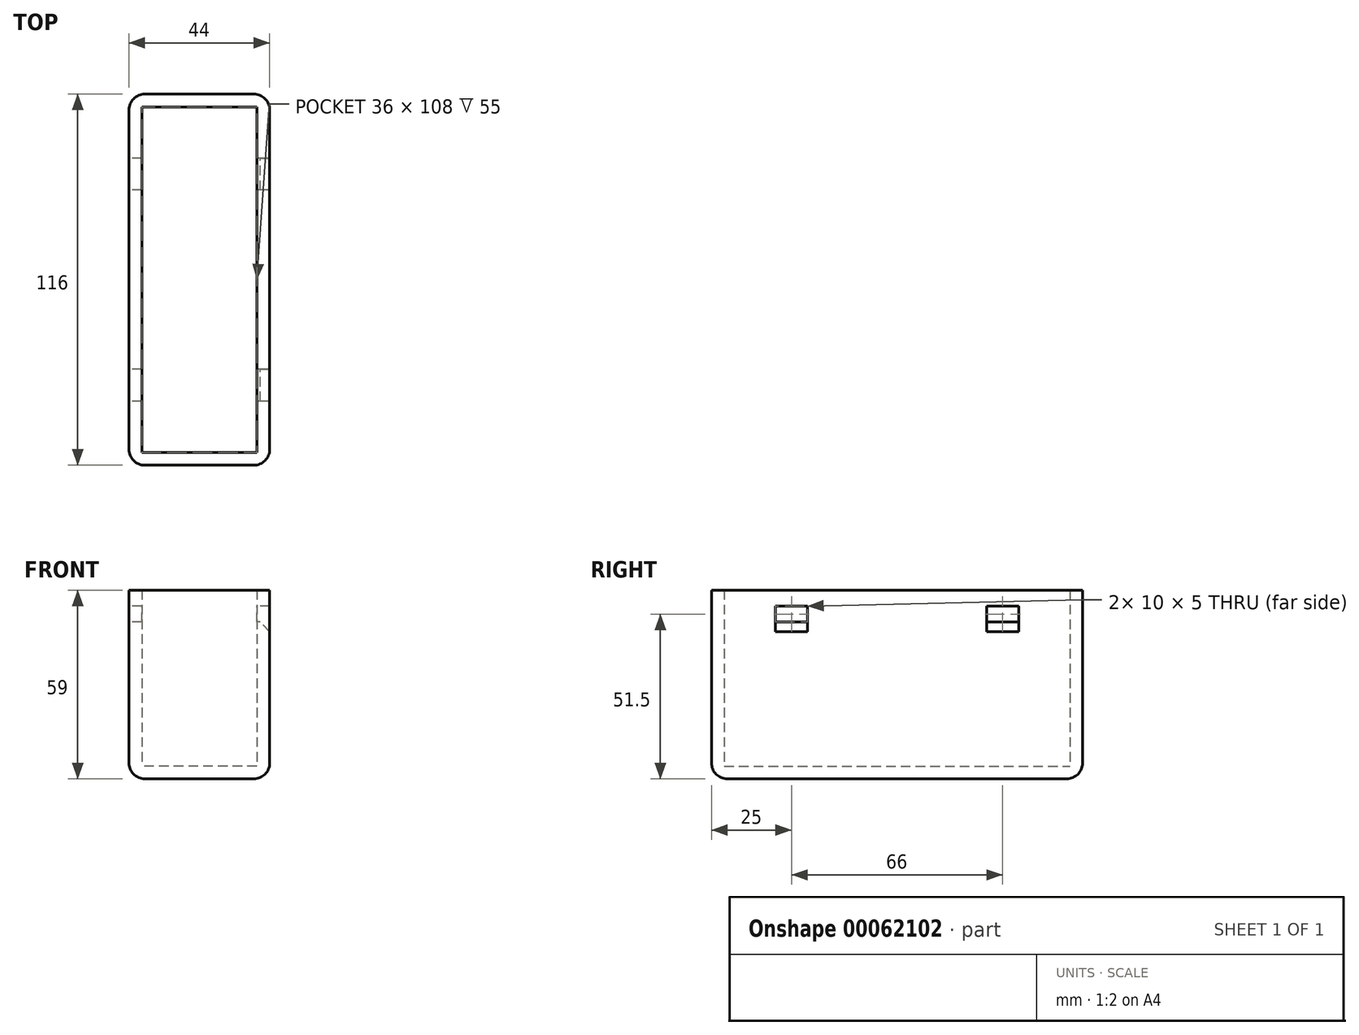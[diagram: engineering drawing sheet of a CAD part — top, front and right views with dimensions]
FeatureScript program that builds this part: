
annotation { "Feature Type Name" : "Feature", "Feature Type Description" : "" }
export const myFeature = defineFeature(function(context is Context, id is Id, definition is map)
    precondition{}
    {
        {
            var Q0;
            Q0=qCreatedBy(makeId("Top.planeOp"),FACE);
            var sketch = newSketch(context, id + "F0", { "sketchPlane" : qUnion([Q0])});
            skLineSegment(sketch, "E0.rect.bottom", {"start": v(18, -54) * mm, "end": v(-18, -54) * mm});
            skLineSegment(sketch, "E0.rect.top", {"start": v(18, 54) * mm, "end": v(-18, 54) * mm});
            skLineSegment(sketch, "E0.rect.left", {"start": v(18, -54) * mm, "end": v(18, 54) * mm});
            skLineSegment(sketch, "E0.rect.right", {"start": v(-18, -54) * mm, "end": v(-18, 54) * mm});
            skPoint(sketch, "E0.rect.middle", {"position": v(0, 0) * mm});
            skSolve(sketch);
        }
        {
            var Q0;
            Q0=makeQuery(id+"F0.imprint","IMPRINT",FACE,{"disambiguationData":[TD([[makeQuery(id+"F0.imprint","IMPRINT",EDGE,{"derivedFrom":sQuery(id+"F0.wireOp",EDGE,"E0.rect.bottom")}),-1.0]])]});
            extrude(context, id + "F1", {"entities" : qUnion([Q0]), "depth" : 55 * mm});
        }
        {
            var Q0;
            Q0=makeQuery(id+"F1.opExtrude","CAP_FACE",FACE,{"disambiguationData":[OSD([sQuery(id+"F0.wireOp",EDGE,"E0.rect.bottom"),sQuery(id+"F0.wireOp",EDGE,"E0.rect.top"),sQuery(id+"F0.wireOp",EDGE,"E0.rect.left"),sQuery(id+"F0.wireOp",EDGE,"E0.rect.right")])],"isStart":false});
            shell(context, id + "F2", {"entities" : qUnion([Q0]), "thickness" : 4 * mm, "oppositeDirection" : true});
        }
        {
            var Q0;
            Q0=makeQuery(id+"F1.opExtrude","SWEPT_EDGE",EDGE,{"disambiguationData":[OSD([sQuery(id+"F0.wireOp",EDGE,"E0.rect.bottom"),sQuery(id+"F0.wireOp",EDGE,"E0.rect.right")])]});
            var Q1;
            Q1=makeQuery(id+"F1.opExtrude","SWEPT_EDGE",EDGE,{"disambiguationData":[OSD([sQuery(id+"F0.wireOp",EDGE,"E0.rect.bottom"),sQuery(id+"F0.wireOp",EDGE,"E0.rect.left")])]});
            var Q2;
            Q2=makeQuery(id+"F1.opExtrude","SWEPT_EDGE",EDGE,{"disambiguationData":[OSD([sQuery(id+"F0.wireOp",EDGE,"E0.rect.top"),sQuery(id+"F0.wireOp",EDGE,"E0.rect.right")])]});
            var Q3;
            Q3=makeQuery(id+"F1.opExtrude","SWEPT_EDGE",EDGE,{"disambiguationData":[OSD([sQuery(id+"F0.wireOp",EDGE,"E0.rect.top"),sQuery(id+"F0.wireOp",EDGE,"E0.rect.left")])]});
            var Q4;
            Q4=makeQuery(id+"F1.opExtrude","CAP_FACE",FACE,{"disambiguationData":[OSD([sQuery(id+"F0.wireOp",EDGE,"E0.rect.bottom"),sQuery(id+"F0.wireOp",EDGE,"E0.rect.top"),sQuery(id+"F0.wireOp",EDGE,"E0.rect.left"),sQuery(id+"F0.wireOp",EDGE,"E0.rect.right")])],"isStart":true});
            fillet(context, id + "F3", {"entities" : qUnion([Q0, Q1, Q2, Q3, Q4]), "radius" : 5 * mm, "tangentPropagation" : true, "allowEdgeOverflow" : false});
        }
        {
            var Q0;
            Q0=makeQuery(id+"F1.opExtrude","SWEPT_FACE",FACE,{"disambiguationData":[OSD([sQuery(id+"F0.wireOp",EDGE,"E0.rect.right")])]});
            var sketch = newSketch(context, id + "F4", { "sketchPlane" : qUnion([Q0])});
            skLineSegment(sketch, "E1.rect.bottom", {"start": v(-28, 45) * mm, "end": v(-38, 45) * mm});
            skLineSegment(sketch, "E1.rect.top", {"start": v(-28, 50) * mm, "end": v(-38, 50) * mm});
            skLineSegment(sketch, "E1.rect.left", {"start": v(-28, 45) * mm, "end": v(-28, 50) * mm});
            skLineSegment(sketch, "E1.rect.right", {"start": v(-38, 45) * mm, "end": v(-38, 50) * mm});
            skPoint(sketch, "E1.rect.middle", {"position": v(-33, 47.5) * mm});
            skLineSegment(sketch, "E2.rect.bottom", {"start": v(38, 45) * mm, "end": v(28, 45) * mm});
            skLineSegment(sketch, "E2.rect.top", {"start": v(38, 50) * mm, "end": v(28, 50) * mm});
            skLineSegment(sketch, "E2.rect.left", {"start": v(38, 45) * mm, "end": v(38, 50) * mm});
            skLineSegment(sketch, "E2.rect.right", {"start": v(28, 45) * mm, "end": v(28, 50) * mm});
            skPoint(sketch, "E2.rect.middle", {"position": v(33, 47.5) * mm});
            skSolve(sketch);
        }
        {
            var Q0;
            Q0=makeQuery(id+"F4.imprint","IMPRINT",FACE,{"disambiguationData":[TD([[makeQuery(id+"F4.imprint","IMPRINT",EDGE,{"derivedFrom":sQuery(id+"F4.wireOp",EDGE,"E1.rect.bottom")}),-1.0]])]});
            var Q1;
            Q1=makeQuery(id+"F4.imprint","IMPRINT",FACE,{"disambiguationData":[TD([[makeQuery(id+"F4.imprint","IMPRINT",EDGE,{"derivedFrom":sQuery(id+"F4.wireOp",EDGE,"E2.rect.bottom")}),-1.0]])]});
            extrude(context, id + "F5", {"entities" : qUnion([Q0, Q1]), "operationType" : NewBodyOperationType.REMOVE, "endBound" : BoundingType.THROUGH_ALL, "oppositeDirection" : true, "depth" : 25 * mm});
        }
        {
            var Q0;
            Q0=makeQuery(id+"F5.boolean.opBoolean","COPY",EDGE,{"derivedFrom":makeQuery(id+"F5.opExtrude","CAP_EDGE",EDGE,{"disambiguationData":[OSD([sQuery(id+"F4.wireOp",EDGE,"E1.rect.bottom")])],"isStart":true})});
            var Q1;
            Q1=makeQuery(id+"F5.boolean.opBoolean","COPY",EDGE,{"derivedFrom":makeQuery(id+"F5.opExtrude","CAP_EDGE",EDGE,{"disambiguationData":[OSD([sQuery(id+"F4.wireOp",EDGE,"E2.rect.bottom")])],"isStart":true})});
            var Q2;
            Q2=makeQuery(id+"F5.boolean.opBoolean","INTERSECT",EDGE,{"derivedFrom":[makeQuery(id+"F1.opExtrude","SWEPT_FACE",FACE,{"disambiguationData":[OSD([sQuery(id+"F0.wireOp",EDGE,"E0.rect.left")])]}),makeQuery(id+"F5.opExtrude","SWEPT_FACE",FACE,{"disambiguationData":[OSD([sQuery(id+"F4.wireOp",EDGE,"E2.rect.bottom")])]})]});
            var Q3;
            Q3=makeQuery(id+"F5.boolean.opBoolean","INTERSECT",EDGE,{"derivedFrom":[makeQuery(id+"F1.opExtrude","SWEPT_FACE",FACE,{"disambiguationData":[OSD([sQuery(id+"F0.wireOp",EDGE,"E0.rect.left")])]}),makeQuery(id+"F5.opExtrude","SWEPT_FACE",FACE,{"disambiguationData":[OSD([sQuery(id+"F4.wireOp",EDGE,"E1.rect.bottom")])]})]});
            chamfer(context, id + "F6", {"entities" : qUnion([Q0, Q1, Q2, Q3]), "width" : 3 * mm, "tangentPropagation" : true});
        }
    });
